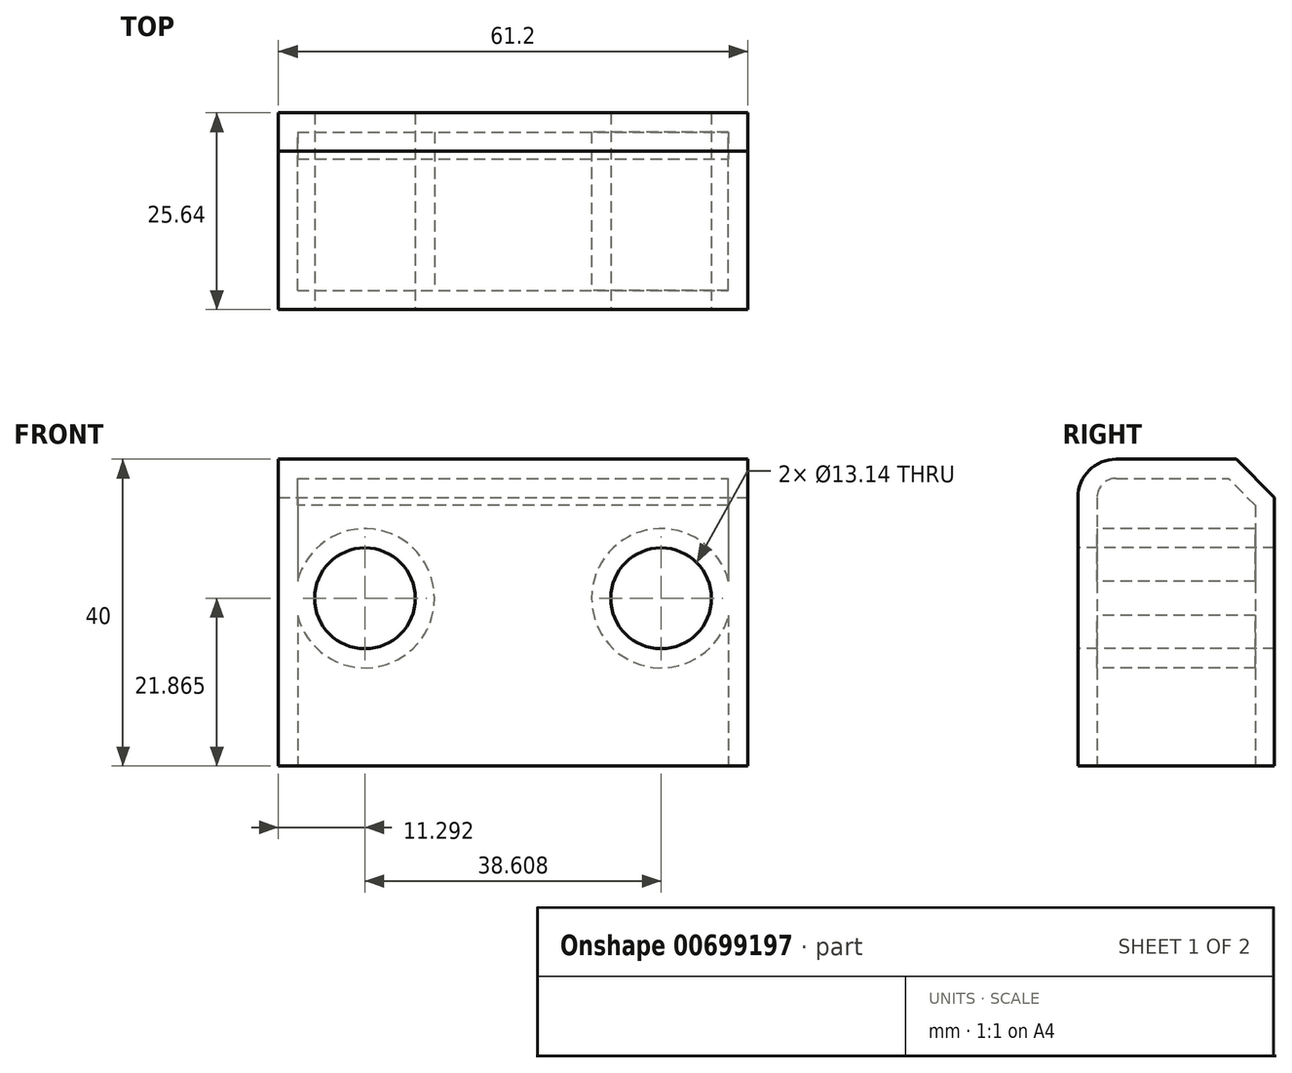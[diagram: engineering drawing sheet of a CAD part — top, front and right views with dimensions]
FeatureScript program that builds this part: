
annotation { "Feature Type Name" : "Feature", "Feature Type Description" : "" }
export const myFeature = defineFeature(function(context is Context, id is Id, definition is map)
    precondition{}
    {
        {
            var Q0;
            Q0=qCreatedBy(makeId("Top.planeOp"),FACE);
            var sketch = newSketch(context, id + "F0", { "sketchPlane" : qUnion([Q0])});
            skLineSegment(sketch, "E0.bottom", {"start": v(-16.32, -10.09) * mm, "end": v(14.28, -10.09) * mm});
            skLineSegment(sketch, "E0.top", {"start": v(-16.32, 15.55) * mm, "end": v(14.28, 15.55) * mm});
            skLineSegment(sketch, "E0.left", {"start": v(-16.32, -10.09) * mm, "end": v(-16.32, 15.55) * mm});
            skLineSegment(sketch, "E0.right", {"start": v(14.28, -10.09) * mm, "end": v(14.28, 15.55) * mm});
            skSolve(sketch);
        }
        {
            var Q0;
            Q0 = qSketchRegion(id + "F0", true);
            extrude(context, id + "F1", {"entities" : qUnion([Q0]), "depth" : 40 * mm, "offsetDistance" : 25 * mm});
        }
        {
            var Q0;
            Q0=makeQuery(id+"F1.opExtrude","SWEPT_FACE",FACE,{"disambiguationData":[OSD([sQuery(id+"F0.wireOp",EDGE,"E0.bottom")])]});
            var sketch = newSketch(context, id + "F2", { "sketchPlane" : qUnion([Q0])});
            skCircle(sketch, "E1", {"center": v(-5.03, 21.86) * mm, "radius": 6.57 * mm});
            skSolve(sketch);
        }
        {
            var Q0;
            Q0=makeQuery(id+"F2.imprint","IMPRINT",FACE,{"disambiguationData":[TD([[makeQuery(id+"F2.imprint","IMPRINT",EDGE,{"derivedFrom":sQuery(id+"F2.wireOp",EDGE,"E1")}),1.0]])]});
            extrude(context, id + "F3", {"entities" : qUnion([Q0]), "operationType" : NewBodyOperationType.REMOVE, "endBound" : BoundingType.THROUGH_ALL, "oppositeDirection" : true, "depth" : 25 * mm, "offsetDistance" : 25 * mm});
        }
        {
            var Q0;
            Q0=makeQuery(id+"F1.opExtrude","CAP_EDGE",EDGE,{"disambiguationData":[OSD([sQuery(id+"F0.wireOp",EDGE,"E0.bottom")])],"isStart":false});
            fillet(context, id + "F4", {"entities" : qUnion([Q0]), "radius" : 5 * mm, "tangentPropagation" : true, "allowEdgeOverflow" : false});
        }
        {
            var Q0;
            Q0=makeQuery(id+"F1.opExtrude","CAP_EDGE",EDGE,{"disambiguationData":[OSD([sQuery(id+"F0.wireOp",EDGE,"E0.top")])],"isStart":false});
            chamfer(context, id + "F5", {"entities" : qUnion([Q0]), "width" : 5 * mm, "tangentPropagation" : true});
        }
        {
            var Q0;
            Q0=makeQuery(id+"F1.opExtrude","CAP_FACE",FACE,{"disambiguationData":[OSD([sQuery(id+"F0.wireOp",EDGE,"E0.bottom"),sQuery(id+"F0.wireOp",EDGE,"E0.top"),sQuery(id+"F0.wireOp",EDGE,"E0.left"),sQuery(id+"F0.wireOp",EDGE,"E0.right")])],"isStart":true});
            var Q1;
            Q1=makeQuery(id+"F1.opExtrude","SWEPT_FACE",FACE,{"disambiguationData":[OSD([sQuery(id+"F0.wireOp",EDGE,"E0.right")])]});
            shell(context, id + "F6", {"entities" : qUnion([Q0, Q1]), "thickness" : 2.5 * mm});
        }
        {
            var Q0;
            Q0=makeQuery(id+"F1.opExtrude","SWEPT_BODY",BODY,{"disambiguationData":[OSD([sQuery(id+"F0.wireOp",EDGE,"E0.bottom"),sQuery(id+"F0.wireOp",EDGE,"E0.top"),sQuery(id+"F0.wireOp",EDGE,"E0.left"),sQuery(id+"F0.wireOp",EDGE,"E0.right")])]});
            var Q1;
            Q1=makeQuery(id+"F1.opExtrude","SWEPT_FACE",FACE,{"disambiguationData":[OSD([sQuery(id+"F0.wireOp",EDGE,"E0.right")])]});
            mirror(context, id + "F7", {"operationType" : NewBodyOperationType.ADD, "entities" : qUnion([Q0]), "mirrorPlane" : qUnion([Q1])});
        }
    });
